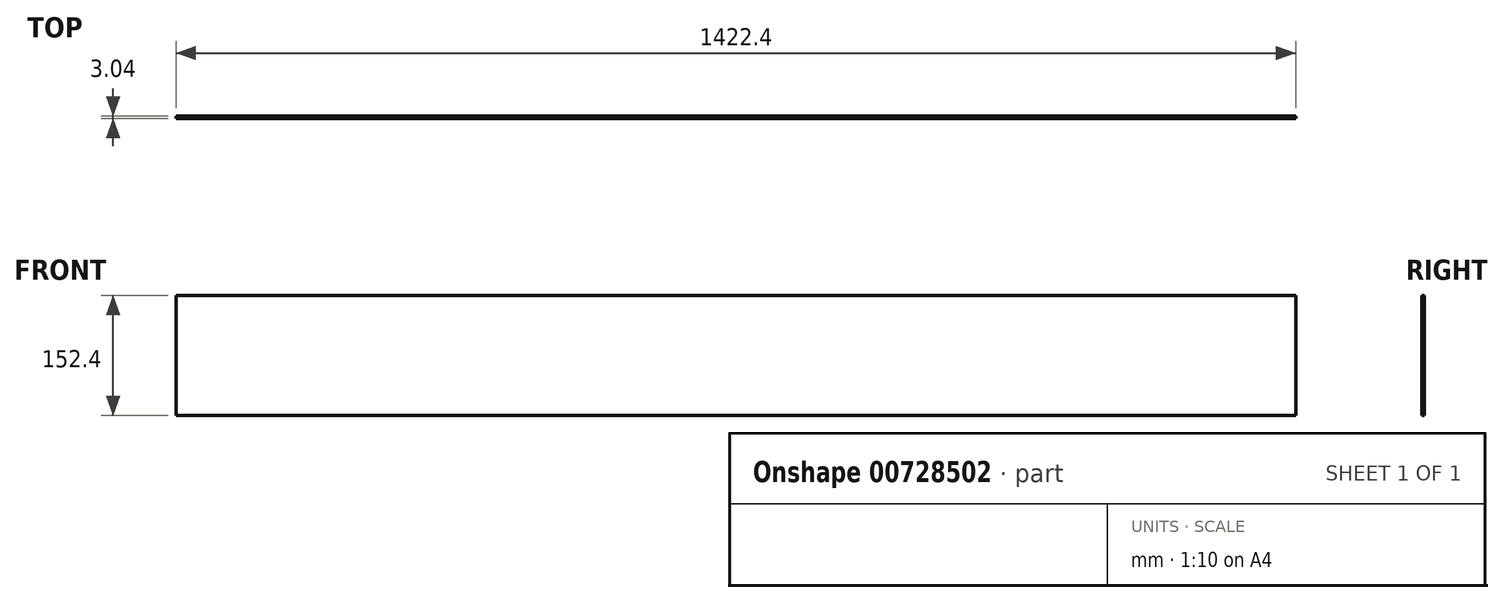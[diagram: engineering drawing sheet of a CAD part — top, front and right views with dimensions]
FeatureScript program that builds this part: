
annotation { "Feature Type Name" : "Feature", "Feature Type Description" : "" }
export const myFeature = defineFeature(function(context is Context, id is Id, definition is map)
    precondition{}
    {
        {
            var Q0;
            Q0=qCreatedBy(makeId("Front.planeOp"),FACE);
            var sketch = newSketch(context, id + "F0", { "sketchPlane" : qUnion([Q0])});
            skLineSegment(sketch, "E0.bottom", {"start": v(-711.2, 76.2) * mm, "end": v(711.2, 76.2) * mm});
            skLineSegment(sketch, "E0.top", {"start": v(-711.2, -76.2) * mm, "end": v(711.2, -76.2) * mm});
            skLineSegment(sketch, "E0.left", {"start": v(-711.2, 76.2) * mm, "end": v(-711.2, -76.2) * mm});
            skLineSegment(sketch, "E0.right", {"start": v(711.2, 76.2) * mm, "end": v(711.2, -76.2) * mm});
            skPoint(sketch, "E0.middle", {"position": v(0, 0) * mm});
            skSolve(sketch);
        }
        {
            var Q0;
            Q0=makeQuery(id+"F0.imprint","IMPRINT",FACE,{"disambiguationData":[TD([[makeQuery(id+"F0.imprint","IMPRINT",EDGE,{"derivedFrom":sQuery(id+"F0.wireOp",EDGE,"E0.bottom")}),-1.0]])]});
            extrude(context, id + "F1", {"entities" : qUnion([Q0]), "endBound" : BoundingType.SYMMETRIC, "depth" : 3.05 * mm, "offsetDistance" : 25.4 * mm});
        }
    });
